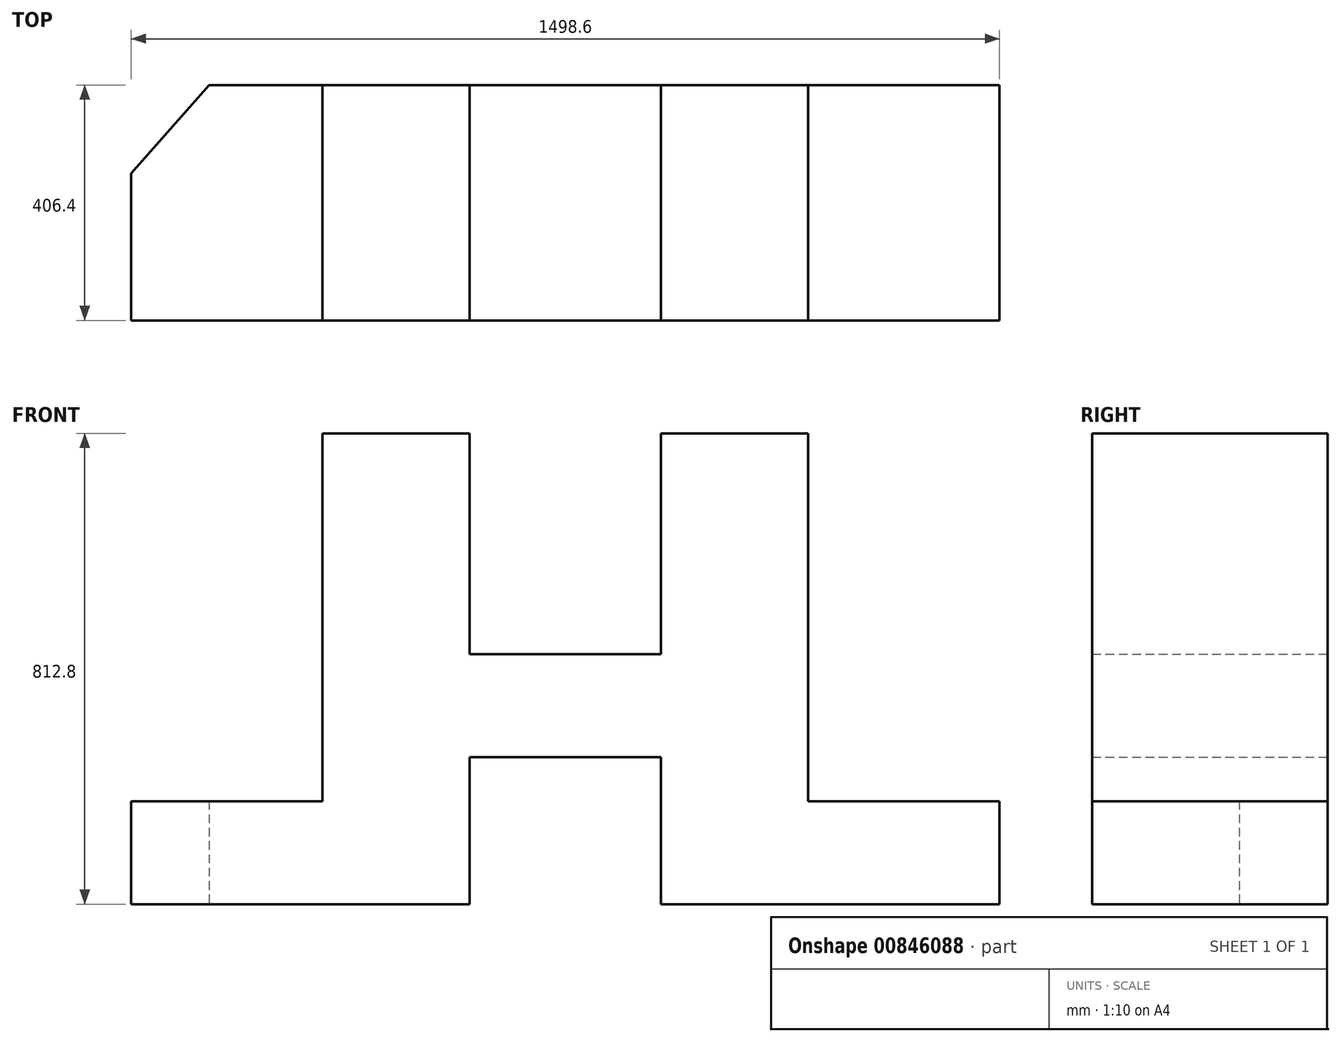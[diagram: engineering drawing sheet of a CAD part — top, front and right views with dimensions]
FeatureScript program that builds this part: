
annotation { "Feature Type Name" : "Feature", "Feature Type Description" : "" }
export const myFeature = defineFeature(function(context is Context, id is Id, definition is map)
    precondition{}
    {
        {
            var Q0;
            Q0=qCreatedBy(makeId("Front.planeOp"),FACE);
            var sketch = newSketch(context, id + "F0", { "sketchPlane" : qUnion([Q0])});
            skLineSegment(sketch, "E0", {"start": v(584.2, 0) * mm, "end": v(584.2, 177.8) * mm});
            skLineSegment(sketch, "E1", {"start": v(584.2, 177.8) * mm, "end": v(254, 177.8) * mm});
            skLineSegment(sketch, "E2", {"start": v(584.2, 0) * mm, "end": v(0, 0) * mm});
            skLineSegment(sketch, "E3", {"start": v(0, 0) * mm, "end": v(0, 254) * mm});
            skLineSegment(sketch, "E4", {"start": v(0, 254) * mm, "end": v(-330.2, 254) * mm});
            skLineSegment(sketch, "E5", {"start": v(-330.2, 254) * mm, "end": v(-330.2, 0) * mm});
            skLineSegment(sketch, "E6", {"start": v(-330.2, 0) * mm, "end": v(-914.4, 0) * mm});
            skLineSegment(sketch, "E7", {"start": v(-914.4, 0) * mm, "end": v(-914.4, 177.8) * mm});
            skLineSegment(sketch, "E8", {"start": v(-914.4, 177.8) * mm, "end": v(-584.2, 177.8) * mm});
            skLineSegment(sketch, "E9", {"start": v(254, 177.8) * mm, "end": v(254, 812.8) * mm});
            skLineSegment(sketch, "E10", {"start": v(-584.2, 177.8) * mm, "end": v(-584.2, 812.8) * mm});
            skLineSegment(sketch, "E11", {"start": v(-584.2, 812.8) * mm, "end": v(-330.2, 812.8) * mm});
            skLineSegment(sketch, "E12", {"start": v(-330.2, 812.8) * mm, "end": v(-330.2, 431.8) * mm});
            skLineSegment(sketch, "E13", {"start": v(-330.2, 431.8) * mm, "end": v(0, 431.8) * mm});
            skLineSegment(sketch, "E14", {"start": v(0, 431.8) * mm, "end": v(0, 812.8) * mm});
            skLineSegment(sketch, "E15", {"start": v(0, 812.8) * mm, "end": v(254, 812.8) * mm});
            skSolve(sketch);
        }
        {
            var Q0;
            Q0 = qSketchRegion(id + "F0", true);
            extrude(context, id + "F1", {"entities" : qUnion([Q0]), "depth" : 406.4 * mm, "offsetDistance" : 25.4 * mm});
        }
        {
            var Q0;
            Q0=makeQuery(id+"F1.opExtrude","SWEPT_FACE",FACE,{"disambiguationData":[OSD([sQuery(id+"F0.wireOp",EDGE,"E6")])]});
            var sketch = newSketch(context, id + "F2", { "sketchPlane" : qUnion([Q0])});
            skLineSegment(sketch, "E16", {"start": v(-914.4, 406.4) * mm, "end": v(-914.4, 152.4) * mm});
            skLineSegment(sketch, "E17", {"start": v(-914.4, 152.4) * mm, "end": v(-780, 0) * mm});
            skSolve(sketch);
        }
        {
            var Q0;
            {var subQ0=sQuery(id+"F2.wireOp",EDGE,"E17");Q0=makeQuery(id+"F2.imprint","IMPRINT",FACE,{"disambiguationData":[TD([[makeQuery(id+"F2.imprint","IMPRINT",EDGE,{"derivedFrom":subQ0}),-1.0]])]});}
            extrude(context, id + "F3", {"entities" : qUnion([Q0]), "operationType" : NewBodyOperationType.REMOVE, "endBound" : BoundingType.THROUGH_ALL, "oppositeDirection" : true, "depth" : 25.4 * mm, "offsetDistance" : 25.4 * mm});
        }
    });
